# Revit family: Lighting - Luminii - Matrix Plus - Dynamic White
name_source: partatom
category: Lighting Fixtures
units: mm (PartAtom-declared; Revit-internal decimal feet)

## family parameters
Cut with Voids When Loaded = No
Host = Face
Light Source = Yes
OmniClass Number = 23.80.70.11.14.21
OmniClass Title = Spots and Tracklight Specialties
Part Type = Normal
Room Calculation Point = No
Round Connector Dimension = Use Diameter
Shared = Yes

## types (2) — shared parameters
Assembly Code = D5020230
CCT = 3000K
Color Filter = 16777215
Current Amps = 50 A
Default Elevation = 0"
Depth = 1/16"
Description = High Efficacy Grid LED panel - 24 VDC
Dimming Lamp Color Temperature Shift = <None>
Emit Shape Visible in Rendering = Yes
Emit from Rectangle Length = 12"
Environment = Indoor
Finish = Metal - Luminii - Silver Anodized Aluminum
Frequency = 60 Hz
Has Battery Backup = No
Has Dimming = Yes
Housing Protection Rating = Consult Manufacturer Website for more Information
Initial Color Comments = Perfomance based on 3000K Photometric Web File
Instruction Sheet Link = https://www.luminii.com
Keynote = 26 50 00
Lamp = LED
Lamp Life = 1
Length = 12"
Lens Material = Plastic - Luminii - Frosted Lens
Load Classification = Lighting
Manufacturer = Luminii
Mounting Method = Surface Mount
Number of Poles = 1
Operating Temperature = Consult Manufacturer Website for more Information
Phase = 1
Power Factor = 1
Power Source Type = Driver
Product Documentation Link = https://www.luminii.com
Product Name = Matrix Plus Dynamic White
Product Page URL = https://www.luminii.com
Tilt Angle = -90.00°
URL = https://www.luminii.com
Version = 2020 - v1.0a
Voltage = 24 V
Voltage Comments = 24 VDC
Warranty URL = https://www.luminii.com

## per-type parameters (varying)
| type | Apparent Load | Constraints | Emit from Rectangle Width | Lumen Output | Model | Photometric Web File | Wattage Comments | Width |
| Matrix Plus DW | 5 VA | 1 | 12" | 228 lm | MP | MP-SO-DW-22K-60K(BOTH)_IESNA2002.IES | 4.6 W | 12" |
| Matrix Mini Plus DW | 1 VA | 2 | 2" | 39 lm | MMP | MMP-SO-DW-22K-60K(BOTH)_IESNA2002.IES | 0.8 W | 2" |

## geometry (parser evidence)
native form markers: Sweep x1
no freeform markers — native parametric forms only
